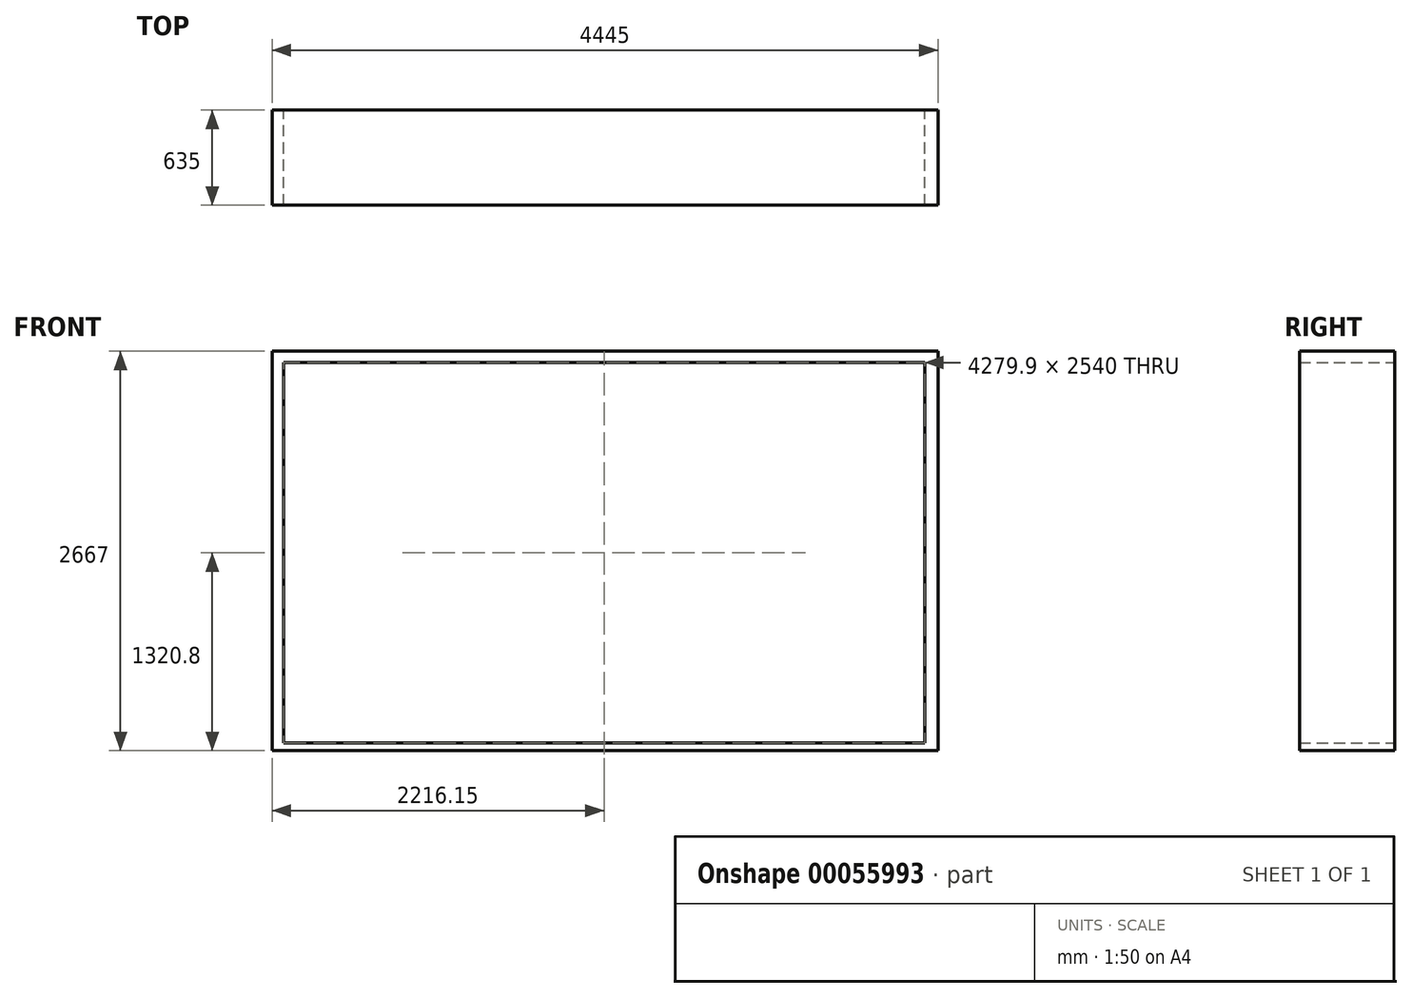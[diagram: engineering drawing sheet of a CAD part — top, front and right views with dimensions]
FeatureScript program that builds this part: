
annotation { "Feature Type Name" : "Feature", "Feature Type Description" : "" }
export const myFeature = defineFeature(function(context is Context, id is Id, definition is map)
    precondition{}
    {
        {
            var Q0;
            Q0=qCreatedBy(makeId("Front.planeOp"),FACE);
            var sketch = newSketch(context, id + "F0", { "sketchPlane" : qUnion([Q0])});
            skLineSegment(sketch, "E0", {"start": v(-1816.1, 673.1) * mm, "end": v(-1816.1, -698.5) * mm});
            skLineSegment(sketch, "E1", {"start": v(-1816.1, -698.5) * mm, "end": v(-127, -698.5) * mm});
            skLineSegment(sketch, "E2", {"start": v(-127, -698.5) * mm, "end": v(-127, 673.1) * mm});
            skLineSegment(sketch, "E3", {"start": v(-127, 673.1) * mm, "end": v(-1816.1, 673.1) * mm});
            skLineSegment(sketch, "E4", {"start": v(-1892.3, 749.3) * mm, "end": v(-1892.3, -774.7) * mm});
            skLineSegment(sketch, "E5", {"start": v(-50.8, -774.7) * mm, "end": v(-50.8, 749.3) * mm});
            skLineSegment(sketch, "E6", {"start": v(-50.8, 749.3) * mm, "end": v(-50.8, 977.9) * mm});
            skLineSegment(sketch, "E7", {"start": v(-50.8, 977.9) * mm, "end": v(1244.6, 977.9) * mm});
            skLineSegment(sketch, "E8", {"start": v(1244.6, 977.9) * mm, "end": v(1244.6, -1003.3) * mm});
            skLineSegment(sketch, "E9", {"start": v(1244.6, -1003.3) * mm, "end": v(-50.8, -1003.3) * mm});
            skLineSegment(sketch, "E10", {"start": v(-50.8, -1003.3) * mm, "end": v(-50.8, -774.7) * mm});
            skLineSegment(sketch, "E11", {"start": v(-127, 749.3) * mm, "end": v(-127, 1054.1) * mm});
            skLineSegment(sketch, "E12", {"start": v(-127, 1054.1) * mm, "end": v(1320.8, 1054.1) * mm});
            skLineSegment(sketch, "E13", {"start": v(1320.8, -1079.5) * mm, "end": v(-127, -1079.5) * mm});
            skLineSegment(sketch, "E14", {"start": v(-1892.3, 749.3) * mm, "end": v(-127, 749.3) * mm});
            skLineSegment(sketch, "E15", {"start": v(-127, -1079.5) * mm, "end": v(-127, -774.7) * mm});
            skLineSegment(sketch, "E16", {"start": v(-1892.3, -774.7) * mm, "end": v(-127, -774.7) * mm});
            skLineSegment(sketch, "E17", {"start": v(1320.8, 254) * mm, "end": v(1930.4, 254) * mm});
            skLineSegment(sketch, "E18", {"start": v(1930.4, 254) * mm, "end": v(1930.4, -279.4) * mm});
            skLineSegment(sketch, "E19", {"start": v(1930.4, -279.4) * mm, "end": v(1320.8, -279.4) * mm});
            skLineSegment(sketch, "E20", {"start": v(1320.8, 330.2) * mm, "end": v(2006.6, 330.2) * mm});
            skLineSegment(sketch, "E21", {"start": v(2006.6, 330.2) * mm, "end": v(2006.6, -355.6) * mm});
            skLineSegment(sketch, "E22", {"start": v(2006.6, -355.6) * mm, "end": v(1320.8, -355.6) * mm});
            skLineSegment(sketch, "E23", {"start": v(1320.8, 1054.1) * mm, "end": v(1320.8, 330.2) * mm});
            skLineSegment(sketch, "E24", {"start": v(1320.8, -355.6) * mm, "end": v(1320.8, -1079.5) * mm});
            skLineSegment(sketch, "E25", {"start": v(1320.8, 254) * mm, "end": v(1320.8, -279.4) * mm});
            skLineSegment(sketch, "E26", {"start": v(596.9, 1257.3) * mm, "end": v(2006.6, 1257.3) * mm});
            skLineSegment(sketch, "E27", {"start": v(2006.6, 1257.3) * mm, "end": v(2133.6, 1257.3) * mm});
            skLineSegment(sketch, "E28", {"start": v(2133.6, 1257.3) * mm, "end": v(2133.6, -1282.7) * mm});
            skLineSegment(sketch, "E29", {"start": v(596.9, 1257.3) * mm, "end": v(-1892.3, 1257.3) * mm});
            skLineSegment(sketch, "E30", {"start": v(-1892.3, 1257.3) * mm, "end": v(-2146.3, 1257.3) * mm});
            skLineSegment(sketch, "E31", {"start": v(-2146.3, 1257.3) * mm, "end": v(-2146.3, -1282.7) * mm});
            skLineSegment(sketch, "E32", {"start": v(-2146.3, -1282.7) * mm, "end": v(2133.6, -1282.7) * mm});
            skLineSegment(sketch, "E33", {"start": v(2222.5, 1333.5) * mm, "end": v(2222.5, -1333.5) * mm});
            skLineSegment(sketch, "E34", {"start": v(-2222.5, -1333.5) * mm, "end": v(2222.5, -1333.5) * mm});
            skLineSegment(sketch, "E35", {"start": v(2222.5, 1333.5) * mm, "end": v(-2222.5, 1333.5) * mm});
            skLineSegment(sketch, "E36", {"start": v(-2222.5, 1333.5) * mm, "end": v(-2222.5, -1333.5) * mm});
            skSolve(sketch);
        }
        {
            var Q0;
            Q0=makeQuery(id+"F0.imprint","IMPRINT",FACE,{"disambiguationData":[TD([[makeQuery(id+"F0.imprint","IMPRINT",EDGE,{"derivedFrom":sQuery(id+"F0.wireOp",EDGE,"E26")}),1.0]])]});
            extrude(context, id + "F1", {"entities" : qUnion([Q0]), "depth" : 635 * mm});
        }
    });
